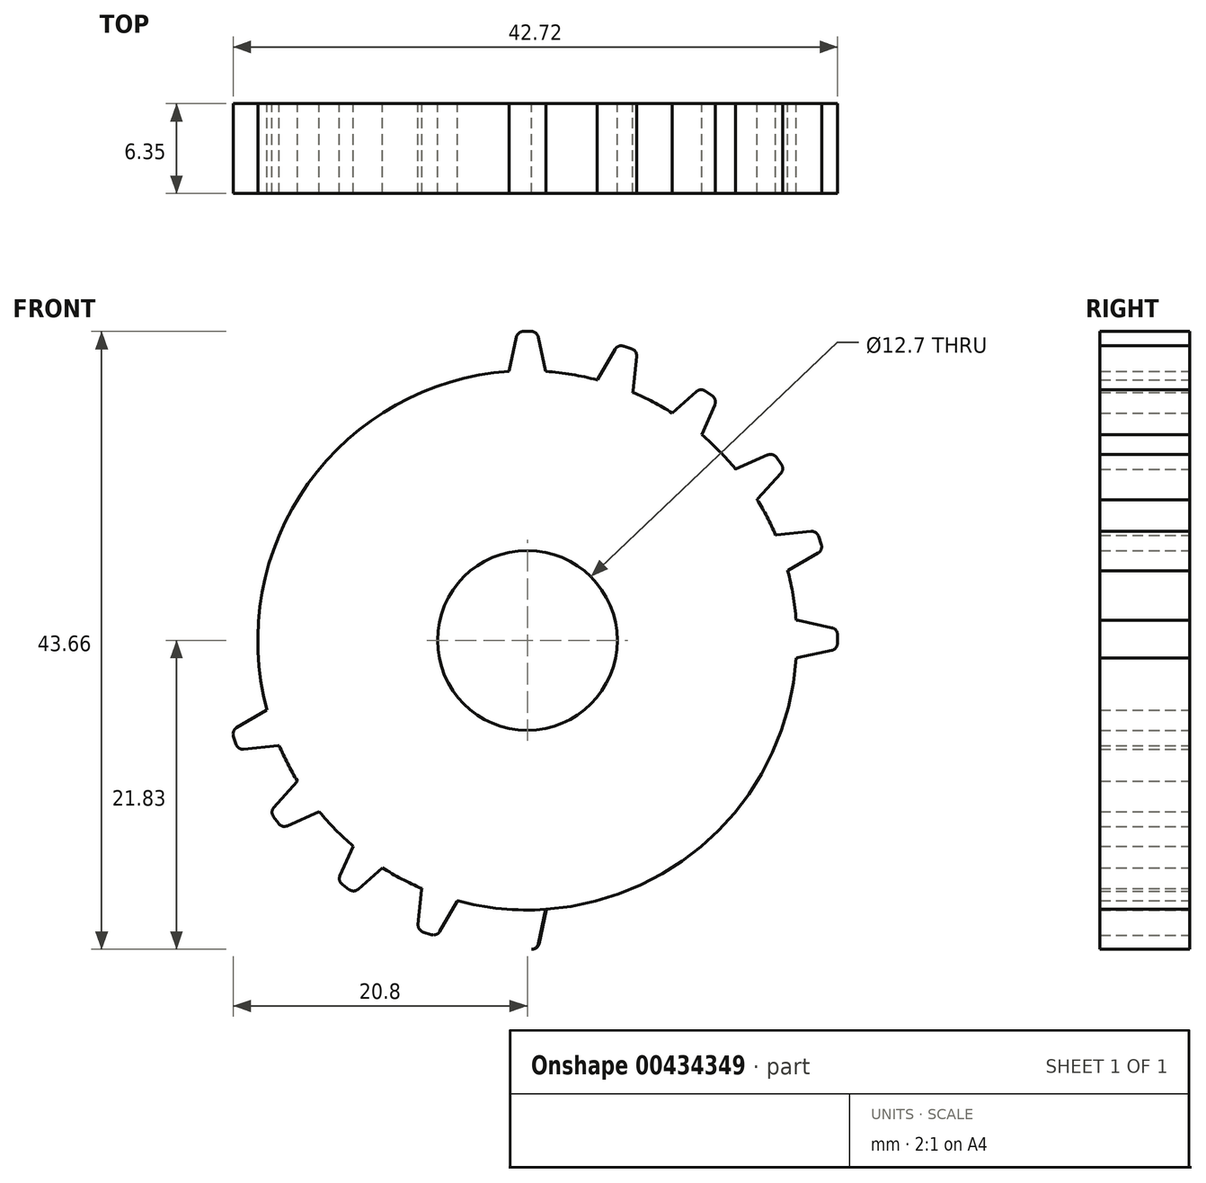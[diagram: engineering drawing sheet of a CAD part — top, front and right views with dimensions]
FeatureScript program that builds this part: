
annotation { "Feature Type Name" : "Feature", "Feature Type Description" : "" }
export const myFeature = defineFeature(function(context is Context, id is Id, definition is map)
    precondition{}
    {
        {
            var Q0;
            Q0=qCreatedBy(makeId("Front.planeOp"),FACE);
            var sketch = newSketch(context, id + "F0", { "sketchPlane" : qUnion([Q0])});
            skCircle(sketch, "E0", {"center": v(0, 0) * mm, "radius": 19.05 * mm});
            skCircle(sketch, "E1", {"center": v(0, 0) * mm, "radius": 6.35 * mm});
            skLineSegment(sketch, "E2", {"start": v(-19.05, 0) * mm, "end": v(19.05, 0) * mm, "construction": true});
            skLineSegment(sketch, "E3", {"start": v(0, 19.05) * mm, "end": v(0, -19.05) * mm, "construction": true});
            skSolve(sketch);
        }
        {
            var Q0;
            Q0 = qSketchRegion(id + "F0", true);
            extrude(context, id + "F1", {"entities" : qUnion([Q0]), "depth" : 6.35 * mm});
        }
        {
            var Q0;
            Q0=qCreatedBy(makeId("Front.planeOp"),FACE);
            var sketch = newSketch(context, id + "F2", { "sketchPlane" : qUnion([Q0])});
            skLineSegment(sketch, "E4", {"start": v(41.5, 29.9) * mm, "end": v(42.1, 29.9) * mm});
            skLineSegment(sketch, "E5", {"start": v(40.48, 27.1) * mm, "end": v(41, 29.5) * mm});
            skLineSegment(sketch, "E6.MirrorCS", {"start": v(43.12, 27.1) * mm, "end": v(42.6, 29.5) * mm});
            skLineSegment(sketch, "E7", {"start": v(40.98, 26.49) * mm, "end": v(42.62, 26.49) * mm});
            skPoint(sketch, "E8.visualSharp", {"position": v(41.08, 29.9) * mm});
            skArc(sketch, "E8.filletArc", {"start": v(41.5, 29.9) * mm, "mid": v(41.18, 29.79) * mm, "end": v(41, 29.5) * mm});
            skPoint(sketch, "E9.visualSharp", {"position": v(42.51, 29.9) * mm});
            skArc(sketch, "E9.filletArc", {"start": v(42.6, 29.5) * mm, "mid": v(42.42, 29.79) * mm, "end": v(42.1, 29.9) * mm});
            skPoint(sketch, "E10.visualSharp", {"position": v(43.25, 26.49) * mm});
            skArc(sketch, "E10.filletArc", {"start": v(42.62, 26.49) * mm, "mid": v(43.02, 26.68) * mm, "end": v(43.12, 27.1) * mm});
            skPoint(sketch, "E11.visualSharp", {"position": v(40.35, 26.49) * mm});
            skArc(sketch, "E11.filletArc", {"start": v(40.48, 27.1) * mm, "mid": v(40.58, 26.68) * mm, "end": v(40.98, 26.49) * mm});
            skLineSegment(sketch, "E12", {"start": v(42.38, 6) * mm, "end": v(42.38, 5.39) * mm});
            skLineSegment(sketch, "E13", {"start": v(39.58, 7.01) * mm, "end": v(41.98, 6.5) * mm});
            skLineSegment(sketch, "E14.MirrorCS", {"start": v(39.58, 4.37) * mm, "end": v(41.98, 4.9) * mm});
            skLineSegment(sketch, "E15", {"start": v(38.97, 6.52) * mm, "end": v(38.97, 4.87) * mm});
            skPoint(sketch, "E16.visualSharp", {"position": v(42.38, 6.4) * mm});
            skArc(sketch, "E16.filletArc", {"start": v(42.38, 6) * mm, "mid": v(42.27, 6.32) * mm, "end": v(41.98, 6.5) * mm});
            skPoint(sketch, "E17.visualSharp", {"position": v(42.38, 4.98) * mm});
            skArc(sketch, "E17.filletArc", {"start": v(41.98, 4.9) * mm, "mid": v(42.27, 5.07) * mm, "end": v(42.38, 5.39) * mm});
            skPoint(sketch, "E18.visualSharp", {"position": v(38.97, 4.24) * mm});
            skArc(sketch, "E18.filletArc", {"start": v(38.97, 4.87) * mm, "mid": v(39.16, 4.48) * mm, "end": v(39.58, 4.37) * mm});
            skPoint(sketch, "E19.visualSharp", {"position": v(38.97, 7.15) * mm});
            skArc(sketch, "E19.filletArc", {"start": v(39.58, 7.01) * mm, "mid": v(39.16, 6.91) * mm, "end": v(38.97, 6.52) * mm});
            skArc(sketch, "E20.MirrorCS", {"start": v(20.55, -6.17) * mm, "mid": v(20.77, -6.43) * mm, "end": v(20.77, -6.77) * mm});
            skArc(sketch, "E21.MirrorCS", {"start": v(6.8, -20.8) * mm, "mid": v(6.45, -20.79) * mm, "end": v(6.2, -20.57) * mm});
            skArc(sketch, "E22.MirrorCS", {"start": v(17.6, -12.94) * mm, "mid": v(17.31, -13.13) * mm, "end": v(16.97, -13.1) * mm});
            skLineSegment(sketch, "E23.MirrorCS", {"start": v(-0.33, -21.83) * mm, "end": v(0.28, -21.83) * mm});
            skLineSegment(sketch, "E24.MirrorCS", {"start": v(17.6, -12.94) * mm, "end": v(17.95, -12.44) * mm});
            skArc(sketch, "E25.MirrorCS", {"start": v(7.72, -20.07) * mm, "mid": v(7.64, -20.4) * mm, "end": v(7.37, -20.6) * mm});
            skArc(sketch, "E26.MirrorCS", {"start": v(17.92, -11.8) * mm, "mid": v(18.04, -12.12) * mm, "end": v(17.95, -12.44) * mm});
            skArc(sketch, "E27.MirrorCS", {"start": v(12.59, -17.61) * mm, "mid": v(12.26, -17.7) * mm, "end": v(11.95, -17.58) * mm});
            skArc(sketch, "E28.MirrorCS", {"start": v(0.78, -21.43) * mm, "mid": v(0.6, -21.72) * mm, "end": v(0.28, -21.83) * mm});
            skArc(sketch, "E29.MirrorCS", {"start": v(-0.33, -21.83) * mm, "mid": v(-0.64, -21.72) * mm, "end": v(-0.82, -21.43) * mm});
            skArc(sketch, "E30.MirrorCS", {"start": v(20.59, -7.35) * mm, "mid": v(20.38, -7.62) * mm, "end": v(20.05, -7.7) * mm});
            skArc(sketch, "E31.MirrorCS", {"start": v(13.25, -16.64) * mm, "mid": v(13.27, -16.98) * mm, "end": v(13.08, -17.25) * mm});
            skLineSegment(sketch, "E32.MirrorCS", {"start": v(20.59, -7.35) * mm, "end": v(20.77, -6.77) * mm});
            skLineSegment(sketch, "E33.MirrorCS", {"start": v(12.59, -17.61) * mm, "end": v(13.08, -17.25) * mm});
            skLineSegment(sketch, "E34.MirrorCS", {"start": v(6.8, -20.8) * mm, "end": v(7.37, -20.6) * mm});
            skArc(sketch, "E35.MirrorCS", {"start": v(17.7, -5.22) * mm, "mid": v(18, -4.9) * mm, "end": v(18.43, -4.94) * mm});
            skLineSegment(sketch, "E36.MirrorCS", {"start": v(14.53, -11.35) * mm, "end": v(15.5, -10.02) * mm});
            skLineSegment(sketch, "E37.MirrorCS", {"start": v(10.16, -15.16) * mm, "end": v(11.5, -14.2) * mm});
            skArc(sketch, "E38.MirrorCS", {"start": v(-1.34, -19.03) * mm, "mid": v(-1.24, -18.6) * mm, "end": v(-0.84, -18.42) * mm});
            skArc(sketch, "E39.MirrorCS", {"start": v(11.5, -14.2) * mm, "mid": v(11.92, -14.11) * mm, "end": v(12.26, -14.4) * mm});
            skArc(sketch, "E40.MirrorCS", {"start": v(0.8, -18.42) * mm, "mid": v(1.2, -18.6) * mm, "end": v(1.3, -19.03) * mm});
            skLineSegment(sketch, "E41.MirrorCS", {"start": v(5.25, -17.71) * mm, "end": v(6.81, -17.2) * mm});
            skLineSegment(sketch, "E42.MirrorCS", {"start": v(17.18, -6.79) * mm, "end": v(17.7, -5.22) * mm});
            skArc(sketch, "E43.MirrorCS", {"start": v(4.96, -18.45) * mm, "mid": v(4.93, -18.01) * mm, "end": v(5.25, -17.71) * mm});
            skArc(sketch, "E44.MirrorCS", {"start": v(15.5, -10.02) * mm, "mid": v(15.88, -9.81) * mm, "end": v(16.28, -9.98) * mm});
            skArc(sketch, "E45.MirrorCS", {"start": v(6.81, -17.2) * mm, "mid": v(7.24, -17.26) * mm, "end": v(7.47, -17.63) * mm});
            skArc(sketch, "E46.MirrorCS", {"start": v(10.12, -15.95) * mm, "mid": v(9.95, -15.54) * mm, "end": v(10.16, -15.16) * mm});
            skArc(sketch, "E47.MirrorCS", {"start": v(17.61, -7.45) * mm, "mid": v(17.24, -7.22) * mm, "end": v(17.18, -6.79) * mm});
            skArc(sketch, "E48.MirrorCS", {"start": v(14.73, -12.11) * mm, "mid": v(14.45, -11.78) * mm, "end": v(14.53, -11.35) * mm});
            skPoint(sketch, "E49.MirrorP", {"position": v(1.43, -18.42) * mm});
            skPoint(sketch, "E50.MirrorP", {"position": v(7.4, -17) * mm});
            skPoint(sketch, "E51.MirrorP", {"position": v(12, -13.82) * mm});
            skPoint(sketch, "E52.MirrorP", {"position": v(17.89, -4.63) * mm});
            skPoint(sketch, "E53.MirrorP", {"position": v(15.86, -9.51) * mm});
            skPoint(sketch, "E54.MirrorP", {"position": v(9.65, -15.53) * mm});
            skPoint(sketch, "E55.MirrorP", {"position": v(20.9, -6.38) * mm});
            skLineSegment(sketch, "E56.MirrorCS", {"start": v(12.26, -14.4) * mm, "end": v(13.25, -16.64) * mm});
            skLineSegment(sketch, "E57.MirrorCS", {"start": v(7.47, -17.63) * mm, "end": v(7.72, -20.07) * mm});
            skLineSegment(sketch, "E58.MirrorCS", {"start": v(16.28, -9.98) * mm, "end": v(17.92, -11.8) * mm});
            skLineSegment(sketch, "E59.MirrorCS", {"start": v(10.12, -15.95) * mm, "end": v(11.95, -17.58) * mm});
            skLineSegment(sketch, "E60.MirrorCS", {"start": v(-1.34, -19.03) * mm, "end": v(-0.82, -21.43) * mm});
            skPoint(sketch, "E61.MirrorP", {"position": v(0.7, -21.83) * mm});
            skPoint(sketch, "E62.MirrorP", {"position": v(7.76, -20.48) * mm});
            skPoint(sketch, "E63.MirrorP", {"position": v(18.19, -12.11) * mm});
            skLineSegment(sketch, "E64.MirrorCS", {"start": v(4.96, -18.45) * mm, "end": v(6.2, -20.57) * mm});
            skLineSegment(sketch, "E65.MirrorCS", {"start": v(14.73, -12.11) * mm, "end": v(16.97, -13.1) * mm});
            skPoint(sketch, "E66.MirrorP", {"position": v(-0.74, -21.83) * mm});
            skPoint(sketch, "E67.MirrorP", {"position": v(6.4, -20.92) * mm});
            skPoint(sketch, "E68.MirrorP", {"position": v(17.35, -13.27) * mm});
            skPoint(sketch, "E69.MirrorP", {"position": v(14.16, -11.86) * mm});
            skPoint(sketch, "E70.MirrorP", {"position": v(16.99, -7.39) * mm});
            skLineSegment(sketch, "E71.MirrorCS", {"start": v(-0.84, -18.42) * mm, "end": v(0.8, -18.42) * mm});
            skLineSegment(sketch, "E72.MirrorCS", {"start": v(1.3, -19.03) * mm, "end": v(0.78, -21.43) * mm});
            skLineSegment(sketch, "E73.MirrorCS", {"start": v(17.61, -7.45) * mm, "end": v(20.05, -7.7) * mm});
            skLineSegment(sketch, "E74.MirrorCS", {"start": v(18.43, -4.94) * mm, "end": v(20.55, -6.17) * mm});
            skPoint(sketch, "E75.MirrorP", {"position": v(12.26, -17.85) * mm});
            skPoint(sketch, "E76.MirrorP", {"position": v(20.46, -7.74) * mm});
            skPoint(sketch, "E77.MirrorP", {"position": v(13.41, -17.01) * mm});
            skPoint(sketch, "E78.MirrorP", {"position": v(-1.47, -18.42) * mm});
            skPoint(sketch, "E79.MirrorP", {"position": v(4.65, -17.9) * mm});
            skArc(sketch, "E80.MirrorCS", {"start": v(0.33, -21.83) * mm, "mid": v(0.64, -21.72) * mm, "end": v(0.82, -21.43) * mm});
            skLineSegment(sketch, "E81.MirrorCS", {"start": v(-12.59, -17.61) * mm, "end": v(-13.08, -17.25) * mm});
            skLineSegment(sketch, "E82.MirrorCS", {"start": v(-6.8, -20.8) * mm, "end": v(-7.37, -20.6) * mm});
            skArc(sketch, "E83.MirrorCS", {"start": v(-20.55, -6.17) * mm, "mid": v(-20.77, -6.43) * mm, "end": v(-20.77, -6.77) * mm});
            skArc(sketch, "E84.MirrorCS", {"start": v(-20.59, -7.35) * mm, "mid": v(-20.38, -7.62) * mm, "end": v(-20.05, -7.7) * mm});
            skLineSegment(sketch, "E85.MirrorCS", {"start": v(-17.6, -12.94) * mm, "end": v(-17.95, -12.44) * mm});
            skLineSegment(sketch, "E86.MirrorCS", {"start": v(-20.59, -7.35) * mm, "end": v(-20.77, -6.77) * mm});
            skArc(sketch, "E87.MirrorCS", {"start": v(-17.92, -11.8) * mm, "mid": v(-18.04, -12.12) * mm, "end": v(-17.95, -12.44) * mm});
            skArc(sketch, "E88.MirrorCS", {"start": v(-7.72, -20.07) * mm, "mid": v(-7.64, -20.4) * mm, "end": v(-7.37, -20.6) * mm});
            skArc(sketch, "E89.MirrorCS", {"start": v(-6.8, -20.8) * mm, "mid": v(-6.45, -20.79) * mm, "end": v(-6.2, -20.57) * mm});
            skLineSegment(sketch, "E90.MirrorCS", {"start": v(0.33, -21.83) * mm, "end": v(-0.28, -21.83) * mm});
            skArc(sketch, "E91.MirrorCS", {"start": v(-13.25, -16.64) * mm, "mid": v(-13.27, -16.98) * mm, "end": v(-13.08, -17.25) * mm});
            skArc(sketch, "E92.MirrorCS", {"start": v(-12.59, -17.61) * mm, "mid": v(-12.26, -17.7) * mm, "end": v(-11.95, -17.58) * mm});
            skArc(sketch, "E93.MirrorCS", {"start": v(-0.78, -21.43) * mm, "mid": v(-0.6, -21.72) * mm, "end": v(-0.28, -21.83) * mm});
            skArc(sketch, "E94.MirrorCS", {"start": v(-17.6, -12.94) * mm, "mid": v(-17.31, -13.13) * mm, "end": v(-16.97, -13.1) * mm});
            skArc(sketch, "E95.MirrorCS", {"start": v(-11.5, -14.2) * mm, "mid": v(-11.92, -14.11) * mm, "end": v(-12.26, -14.4) * mm});
            skArc(sketch, "E96.MirrorCS", {"start": v(-14.73, -12.11) * mm, "mid": v(-14.45, -11.78) * mm, "end": v(-14.53, -11.35) * mm});
            skArc(sketch, "E97.MirrorCS", {"start": v(-17.7, -5.22) * mm, "mid": v(-18, -4.9) * mm, "end": v(-18.43, -4.94) * mm});
            skArc(sketch, "E98.MirrorCS", {"start": v(-0.8, -18.42) * mm, "mid": v(-1.2, -18.6) * mm, "end": v(-1.3, -19.03) * mm});
            skLineSegment(sketch, "E99.MirrorCS", {"start": v(-14.53, -11.35) * mm, "end": v(-15.5, -10.02) * mm});
            skArc(sketch, "E100.MirrorCS", {"start": v(-10.12, -15.95) * mm, "mid": v(-9.95, -15.54) * mm, "end": v(-10.16, -15.16) * mm});
            skLineSegment(sketch, "E101.MirrorCS", {"start": v(-10.16, -15.16) * mm, "end": v(-11.5, -14.2) * mm});
            skLineSegment(sketch, "E102.MirrorCS", {"start": v(-17.18, -6.79) * mm, "end": v(-17.7, -5.22) * mm});
            skLineSegment(sketch, "E103.MirrorCS", {"start": v(-5.25, -17.71) * mm, "end": v(-6.81, -17.2) * mm});
            skArc(sketch, "E104.MirrorCS", {"start": v(-6.81, -17.2) * mm, "mid": v(-7.24, -17.26) * mm, "end": v(-7.47, -17.63) * mm});
            skArc(sketch, "E105.MirrorCS", {"start": v(-17.61, -7.45) * mm, "mid": v(-17.24, -7.22) * mm, "end": v(-17.18, -6.79) * mm});
            skArc(sketch, "E106.MirrorCS", {"start": v(-15.5, -10.02) * mm, "mid": v(-15.88, -9.81) * mm, "end": v(-16.28, -9.98) * mm});
            skArc(sketch, "E107.MirrorCS", {"start": v(1.34, -19.03) * mm, "mid": v(1.24, -18.6) * mm, "end": v(0.84, -18.42) * mm});
            skArc(sketch, "E108.MirrorCS", {"start": v(-4.96, -18.45) * mm, "mid": v(-4.93, -18.01) * mm, "end": v(-5.25, -17.71) * mm});
            skLineSegment(sketch, "E109.MirrorCS", {"start": v(-14.73, -12.11) * mm, "end": v(-16.97, -13.1) * mm});
            skPoint(sketch, "E110.MirrorP", {"position": v(-7.76, -20.48) * mm});
            skPoint(sketch, "E111.MirrorP", {"position": v(-13.41, -17.01) * mm});
            skPoint(sketch, "E112.MirrorP", {"position": v(-15.86, -9.51) * mm});
            skPoint(sketch, "E113.MirrorP", {"position": v(-9.65, -15.53) * mm});
            skLineSegment(sketch, "E114.MirrorCS", {"start": v(-12.26, -14.4) * mm, "end": v(-13.25, -16.64) * mm});
            skPoint(sketch, "E115.MirrorP", {"position": v(0.74, -21.83) * mm});
            skLineSegment(sketch, "E116.MirrorCS", {"start": v(-7.47, -17.63) * mm, "end": v(-7.72, -20.07) * mm});
            skPoint(sketch, "E117.MirrorP", {"position": v(-12.26, -17.85) * mm});
            skPoint(sketch, "E118.MirrorP", {"position": v(-6.4, -20.92) * mm});
            skLineSegment(sketch, "E119.MirrorCS", {"start": v(-16.28, -9.98) * mm, "end": v(-17.92, -11.8) * mm});
            skPoint(sketch, "E120.MirrorP", {"position": v(-12, -13.82) * mm});
            skLineSegment(sketch, "E121.MirrorCS", {"start": v(0.84, -18.42) * mm, "end": v(-0.8, -18.42) * mm});
            skPoint(sketch, "E122.MirrorP", {"position": v(-17.35, -13.27) * mm});
            skPoint(sketch, "E123.MirrorP", {"position": v(-20.9, -6.38) * mm});
            skLineSegment(sketch, "E124.MirrorCS", {"start": v(-10.12, -15.95) * mm, "end": v(-11.95, -17.58) * mm});
            skPoint(sketch, "E125.MirrorP", {"position": v(1.47, -18.42) * mm});
            skPoint(sketch, "E126.MirrorP", {"position": v(-14.16, -11.86) * mm});
            skLineSegment(sketch, "E127.MirrorCS", {"start": v(-17.61, -7.45) * mm, "end": v(-20.05, -7.7) * mm});
            skPoint(sketch, "E128.MirrorP", {"position": v(-18.19, -12.11) * mm});
            skPoint(sketch, "E129.MirrorP", {"position": v(-1.43, -18.42) * mm});
            skPoint(sketch, "E130.MirrorP", {"position": v(-20.46, -7.74) * mm});
            skLineSegment(sketch, "E131.MirrorCS", {"start": v(1.34, -19.03) * mm, "end": v(0.82, -21.43) * mm});
            skLineSegment(sketch, "E132.MirrorCS", {"start": v(-1.3, -19.03) * mm, "end": v(-0.78, -21.43) * mm});
            skPoint(sketch, "E133.MirrorP", {"position": v(-7.4, -17) * mm});
            skPoint(sketch, "E134.MirrorP", {"position": v(-0.7, -21.83) * mm});
            skPoint(sketch, "E135.MirrorP", {"position": v(-16.99, -7.39) * mm});
            skLineSegment(sketch, "E136.MirrorCS", {"start": v(-18.43, -4.94) * mm, "end": v(-20.55, -6.17) * mm});
            skLineSegment(sketch, "E137.MirrorCS", {"start": v(-4.96, -18.45) * mm, "end": v(-6.2, -20.57) * mm});
            skPoint(sketch, "E138.MirrorP", {"position": v(-17.89, -4.63) * mm});
            skPoint(sketch, "E139.MirrorP", {"position": v(-4.65, -17.9) * mm});
            skLineSegment(sketch, "E140.MirrorCS", {"start": v(0.33, 21.83) * mm, "end": v(-0.28, 21.83) * mm});
            skArc(sketch, "E141.MirrorCS", {"start": v(0.33, 21.83) * mm, "mid": v(0.64, 21.72) * mm, "end": v(0.82, 21.43) * mm});
            skArc(sketch, "E142.MirrorCS", {"start": v(0.78, 21.43) * mm, "mid": v(0.6, 21.72) * mm, "end": v(0.28, 21.83) * mm});
            skArc(sketch, "E143.MirrorCS", {"start": v(-0.78, 21.43) * mm, "mid": v(-0.6, 21.72) * mm, "end": v(-0.28, 21.83) * mm});
            skArc(sketch, "E144.MirrorCS", {"start": v(-0.33, 21.83) * mm, "mid": v(-0.64, 21.72) * mm, "end": v(-0.82, 21.43) * mm});
            skLineSegment(sketch, "E145.MirrorCS", {"start": v(-0.33, 21.83) * mm, "end": v(0.28, 21.83) * mm});
            skArc(sketch, "E146.MirrorCS", {"start": v(-1.34, 19.03) * mm, "mid": v(-1.24, 18.6) * mm, "end": v(-0.84, 18.42) * mm});
            skArc(sketch, "E147.MirrorCS", {"start": v(-0.8, 18.42) * mm, "mid": v(-1.2, 18.6) * mm, "end": v(-1.3, 19.03) * mm});
            skLineSegment(sketch, "E148.MirrorCS", {"start": v(-0.84, 18.42) * mm, "end": v(0.8, 18.42) * mm});
            skArc(sketch, "E149.MirrorCS", {"start": v(0.8, 18.42) * mm, "mid": v(1.2, 18.6) * mm, "end": v(1.3, 19.03) * mm});
            skLineSegment(sketch, "E150.MirrorCS", {"start": v(0.84, 18.42) * mm, "end": v(-0.8, 18.42) * mm});
            skArc(sketch, "E151.MirrorCS", {"start": v(1.34, 19.03) * mm, "mid": v(1.24, 18.6) * mm, "end": v(0.84, 18.42) * mm});
            skArc(sketch, "E152.MirrorCS", {"start": v(-15.5, 10.02) * mm, "mid": v(-15.88, 9.81) * mm, "end": v(-16.28, 9.98) * mm});
            skArc(sketch, "E153.MirrorCS", {"start": v(17.6, 12.94) * mm, "mid": v(17.31, 13.13) * mm, "end": v(16.97, 13.1) * mm});
            skArc(sketch, "E154.MirrorCS", {"start": v(-7.72, 20.07) * mm, "mid": v(-7.64, 20.4) * mm, "end": v(-7.37, 20.6) * mm});
            skArc(sketch, "E155.MirrorCS", {"start": v(-17.92, 11.8) * mm, "mid": v(-18.04, 12.12) * mm, "end": v(-17.95, 12.44) * mm});
            skArc(sketch, "E156.MirrorCS", {"start": v(20.59, 7.35) * mm, "mid": v(20.38, 7.62) * mm, "end": v(20.05, 7.7) * mm});
            skLineSegment(sketch, "E157.MirrorCS", {"start": v(-6.8, 20.8) * mm, "end": v(-7.37, 20.6) * mm});
            skArc(sketch, "E158.MirrorCS", {"start": v(20.55, 6.17) * mm, "mid": v(20.77, 6.43) * mm, "end": v(20.77, 6.77) * mm});
            skArc(sketch, "E159.MirrorCS", {"start": v(-12.59, 17.61) * mm, "mid": v(-12.26, 17.7) * mm, "end": v(-11.95, 17.58) * mm});
            skArc(sketch, "E160.MirrorCS", {"start": v(6.8, 20.8) * mm, "mid": v(6.45, 20.79) * mm, "end": v(6.2, 20.57) * mm});
            skArc(sketch, "E161.MirrorCS", {"start": v(13.25, 16.64) * mm, "mid": v(13.27, 16.98) * mm, "end": v(13.08, 17.25) * mm});
            skArc(sketch, "E162.MirrorCS", {"start": v(12.59, 17.61) * mm, "mid": v(12.26, 17.7) * mm, "end": v(11.95, 17.58) * mm});
            skLineSegment(sketch, "E163.MirrorCS", {"start": v(12.59, 17.61) * mm, "end": v(13.08, 17.25) * mm});
            skArc(sketch, "E164.MirrorCS", {"start": v(15.5, 10.02) * mm, "mid": v(15.88, 9.81) * mm, "end": v(16.28, 9.98) * mm});
            skArc(sketch, "E165.MirrorCS", {"start": v(-20.55, 6.17) * mm, "mid": v(-20.77, 6.43) * mm, "end": v(-20.77, 6.77) * mm});
            skLineSegment(sketch, "E166.MirrorCS", {"start": v(20.59, 7.35) * mm, "end": v(20.77, 6.77) * mm});
            skArc(sketch, "E167.MirrorCS", {"start": v(-20.59, 7.35) * mm, "mid": v(-20.38, 7.62) * mm, "end": v(-20.05, 7.7) * mm});
            skLineSegment(sketch, "E168.MirrorCS", {"start": v(6.8, 20.8) * mm, "end": v(7.37, 20.6) * mm});
            skLineSegment(sketch, "E169.MirrorCS", {"start": v(17.6, 12.94) * mm, "end": v(17.95, 12.44) * mm});
            skLineSegment(sketch, "E170.MirrorCS", {"start": v(-17.6, 12.94) * mm, "end": v(-17.95, 12.44) * mm});
            skArc(sketch, "E171.MirrorCS", {"start": v(-17.6, 12.94) * mm, "mid": v(-17.31, 13.13) * mm, "end": v(-16.97, 13.1) * mm});
            skLineSegment(sketch, "E172.MirrorCS", {"start": v(-20.59, 7.35) * mm, "end": v(-20.77, 6.77) * mm});
            skArc(sketch, "E173.MirrorCS", {"start": v(17.92, 11.8) * mm, "mid": v(18.04, 12.12) * mm, "end": v(17.95, 12.44) * mm});
            skArc(sketch, "E174.MirrorCS", {"start": v(-13.25, 16.64) * mm, "mid": v(-13.27, 16.98) * mm, "end": v(-13.08, 17.25) * mm});
            skArc(sketch, "E175.MirrorCS", {"start": v(-6.8, 20.8) * mm, "mid": v(-6.45, 20.79) * mm, "end": v(-6.2, 20.57) * mm});
            skArc(sketch, "E176.MirrorCS", {"start": v(-6.81, 17.2) * mm, "mid": v(-7.24, 17.26) * mm, "end": v(-7.47, 17.63) * mm});
            skLineSegment(sketch, "E177.MirrorCS", {"start": v(-5.25, 17.71) * mm, "end": v(-6.81, 17.2) * mm});
            skArc(sketch, "E178.MirrorCS", {"start": v(17.7, 5.22) * mm, "mid": v(18, 4.9) * mm, "end": v(18.43, 4.94) * mm});
            skArc(sketch, "E179.MirrorCS", {"start": v(10.12, 15.95) * mm, "mid": v(9.95, 15.54) * mm, "end": v(10.16, 15.16) * mm});
            skLineSegment(sketch, "E180.MirrorCS", {"start": v(14.53, 11.35) * mm, "end": v(15.5, 10.02) * mm});
            skLineSegment(sketch, "E181.MirrorCS", {"start": v(-14.53, 11.35) * mm, "end": v(-15.5, 10.02) * mm});
            skArc(sketch, "E182.MirrorCS", {"start": v(-11.5, 14.2) * mm, "mid": v(-11.92, 14.11) * mm, "end": v(-12.26, 14.4) * mm});
            skArc(sketch, "E183.MirrorCS", {"start": v(-4.96, 18.45) * mm, "mid": v(-4.93, 18.01) * mm, "end": v(-5.25, 17.71) * mm});
            skArc(sketch, "E184.MirrorCS", {"start": v(-14.73, 12.11) * mm, "mid": v(-14.45, 11.78) * mm, "end": v(-14.53, 11.35) * mm});
            skLineSegment(sketch, "E185.MirrorCS", {"start": v(5.25, 17.71) * mm, "end": v(6.81, 17.2) * mm});
            skArc(sketch, "E186.MirrorCS", {"start": v(7.72, 20.07) * mm, "mid": v(7.64, 20.4) * mm, "end": v(7.37, 20.6) * mm});
            skArc(sketch, "E187.MirrorCS", {"start": v(-10.12, 15.95) * mm, "mid": v(-9.95, 15.54) * mm, "end": v(-10.16, 15.16) * mm});
            skArc(sketch, "E188.MirrorCS", {"start": v(14.73, 12.11) * mm, "mid": v(14.45, 11.78) * mm, "end": v(14.53, 11.35) * mm});
            skArc(sketch, "E189.MirrorCS", {"start": v(-17.61, 7.45) * mm, "mid": v(-17.24, 7.22) * mm, "end": v(-17.18, 6.79) * mm});
            skArc(sketch, "E190.MirrorCS", {"start": v(17.61, 7.45) * mm, "mid": v(17.24, 7.22) * mm, "end": v(17.18, 6.79) * mm});
            skArc(sketch, "E191.MirrorCS", {"start": v(4.96, 18.45) * mm, "mid": v(4.93, 18.01) * mm, "end": v(5.25, 17.71) * mm});
            skLineSegment(sketch, "E192.MirrorCS", {"start": v(10.16, 15.16) * mm, "end": v(11.5, 14.2) * mm});
            skArc(sketch, "E193.MirrorCS", {"start": v(-17.7, 5.22) * mm, "mid": v(-18, 4.9) * mm, "end": v(-18.43, 4.94) * mm});
            skLineSegment(sketch, "E194.MirrorCS", {"start": v(-10.16, 15.16) * mm, "end": v(-11.5, 14.2) * mm});
            skLineSegment(sketch, "E195.MirrorCS", {"start": v(-12.59, 17.61) * mm, "end": v(-13.08, 17.25) * mm});
            skArc(sketch, "E196.MirrorCS", {"start": v(6.81, 17.2) * mm, "mid": v(7.24, 17.26) * mm, "end": v(7.47, 17.63) * mm});
            skLineSegment(sketch, "E197.MirrorCS", {"start": v(-17.18, 6.79) * mm, "end": v(-17.7, 5.22) * mm});
            skLineSegment(sketch, "E198.MirrorCS", {"start": v(17.18, 6.79) * mm, "end": v(17.7, 5.22) * mm});
            skArc(sketch, "E199.MirrorCS", {"start": v(11.5, 14.2) * mm, "mid": v(11.92, 14.11) * mm, "end": v(12.26, 14.4) * mm});
            skPoint(sketch, "E200.MirrorP", {"position": v(0.7, 21.83) * mm});
            skPoint(sketch, "E201.MirrorP", {"position": v(-0.74, 21.83) * mm});
            skPoint(sketch, "E202.MirrorP", {"position": v(-1.47, 18.42) * mm});
            skPoint(sketch, "E203.MirrorP", {"position": v(1.43, 18.42) * mm});
            skLineSegment(sketch, "E204.MirrorCS", {"start": v(-1.3, 19.03) * mm, "end": v(-0.78, 21.43) * mm});
            skPoint(sketch, "E205.MirrorP", {"position": v(17.35, 13.27) * mm});
            skPoint(sketch, "E206.MirrorP", {"position": v(0.74, 21.83) * mm});
            skLineSegment(sketch, "E207.MirrorCS", {"start": v(4.96, 18.45) * mm, "end": v(6.2, 20.57) * mm});
            skLineSegment(sketch, "E208.MirrorCS", {"start": v(10.12, 15.95) * mm, "end": v(11.95, 17.58) * mm});
            skLineSegment(sketch, "E209.MirrorCS", {"start": v(16.28, 9.98) * mm, "end": v(17.92, 11.8) * mm});
            skLineSegment(sketch, "E210.MirrorCS", {"start": v(-4.96, 18.45) * mm, "end": v(-6.2, 20.57) * mm});
            skPoint(sketch, "E211.MirrorP", {"position": v(16.99, 7.39) * mm});
            skPoint(sketch, "E212.MirrorP", {"position": v(-6.4, 20.92) * mm});
            skPoint(sketch, "E213.MirrorP", {"position": v(-4.65, 17.9) * mm});
            skPoint(sketch, "E214.MirrorP", {"position": v(18.19, 12.11) * mm});
            skPoint(sketch, "E215.MirrorP", {"position": v(-13.41, 17.01) * mm});
            skPoint(sketch, "E216.MirrorP", {"position": v(6.4, 20.92) * mm});
            skPoint(sketch, "E217.MirrorP", {"position": v(-9.65, 15.53) * mm});
            skPoint(sketch, "E218.MirrorP", {"position": v(20.9, 6.38) * mm});
            skLineSegment(sketch, "E219.MirrorCS", {"start": v(-10.12, 15.95) * mm, "end": v(-11.95, 17.58) * mm});
            skPoint(sketch, "E220.MirrorP", {"position": v(-7.76, 20.48) * mm});
            skPoint(sketch, "E221.MirrorP", {"position": v(-0.7, 21.83) * mm});
            skPoint(sketch, "E222.MirrorP", {"position": v(7.76, 20.48) * mm});
            skPoint(sketch, "E223.MirrorP", {"position": v(-20.46, 7.74) * mm});
            skPoint(sketch, "E224.MirrorP", {"position": v(-17.35, 13.27) * mm});
            skLineSegment(sketch, "E225.MirrorCS", {"start": v(18.43, 4.94) * mm, "end": v(20.55, 6.17) * mm});
            skLineSegment(sketch, "E226.MirrorCS", {"start": v(-17.61, 7.45) * mm, "end": v(-20.05, 7.7) * mm});
            skLineSegment(sketch, "E227.MirrorCS", {"start": v(-7.47, 17.63) * mm, "end": v(-7.72, 20.07) * mm});
            skPoint(sketch, "E228.MirrorP", {"position": v(-20.9, 6.38) * mm});
            skPoint(sketch, "E229.MirrorP", {"position": v(-18.19, 12.11) * mm});
            skPoint(sketch, "E230.MirrorP", {"position": v(-7.4, 17) * mm});
            skLineSegment(sketch, "E231.MirrorCS", {"start": v(-16.28, 9.98) * mm, "end": v(-17.92, 11.8) * mm});
            skPoint(sketch, "E232.MirrorP", {"position": v(-12.26, 17.85) * mm});
            skPoint(sketch, "E233.MirrorP", {"position": v(14.16, 11.86) * mm});
            skLineSegment(sketch, "E234.MirrorCS", {"start": v(-14.73, 12.11) * mm, "end": v(-16.97, 13.1) * mm});
            skPoint(sketch, "E235.MirrorP", {"position": v(-15.86, 9.51) * mm});
            skPoint(sketch, "E236.MirrorP", {"position": v(-17.89, 4.63) * mm});
            skPoint(sketch, "E237.MirrorP", {"position": v(9.65, 15.53) * mm});
            skPoint(sketch, "E238.MirrorP", {"position": v(1.47, 18.42) * mm});
            skPoint(sketch, "E239.MirrorP", {"position": v(20.46, 7.74) * mm});
            skLineSegment(sketch, "E240.MirrorCS", {"start": v(1.34, 19.03) * mm, "end": v(0.82, 21.43) * mm});
            skPoint(sketch, "E241.MirrorP", {"position": v(4.65, 17.9) * mm});
            skPoint(sketch, "E242.MirrorP", {"position": v(17.89, 4.63) * mm});
            skPoint(sketch, "E243.MirrorP", {"position": v(-14.16, 11.86) * mm});
            skPoint(sketch, "E244.MirrorP", {"position": v(-1.43, 18.42) * mm});
            skPoint(sketch, "E245.MirrorP", {"position": v(-16.99, 7.39) * mm});
            skLineSegment(sketch, "E246.MirrorCS", {"start": v(-18.43, 4.94) * mm, "end": v(-20.55, 6.17) * mm});
            skPoint(sketch, "E247.MirrorP", {"position": v(15.86, 9.51) * mm});
            skLineSegment(sketch, "E248.MirrorCS", {"start": v(1.3, 19.03) * mm, "end": v(0.78, 21.43) * mm});
            skPoint(sketch, "E249.MirrorP", {"position": v(12.26, 17.85) * mm});
            skPoint(sketch, "E250.MirrorP", {"position": v(-12, 13.82) * mm});
            skPoint(sketch, "E251.MirrorP", {"position": v(12, 13.82) * mm});
            skLineSegment(sketch, "E252.MirrorCS", {"start": v(-12.26, 14.4) * mm, "end": v(-13.25, 16.64) * mm});
            skPoint(sketch, "E253.MirrorP", {"position": v(7.4, 17) * mm});
            skPoint(sketch, "E254.MirrorP", {"position": v(13.41, 17.01) * mm});
            skLineSegment(sketch, "E255.MirrorCS", {"start": v(7.47, 17.63) * mm, "end": v(7.72, 20.07) * mm});
            skLineSegment(sketch, "E256.MirrorCS", {"start": v(14.73, 12.11) * mm, "end": v(16.97, 13.1) * mm});
            skLineSegment(sketch, "E257.MirrorCS", {"start": v(12.26, 14.4) * mm, "end": v(13.25, 16.64) * mm});
            skLineSegment(sketch, "E258.MirrorCS", {"start": v(17.61, 7.45) * mm, "end": v(20.05, 7.7) * mm});
            skLineSegment(sketch, "E259.MirrorCS", {"start": v(-1.34, 19.03) * mm, "end": v(-0.82, 21.43) * mm});
            skArc(sketch, "E260.MirrorCS", {"start": v(42.38, -6) * mm, "mid": v(42.27, -6.32) * mm, "end": v(41.98, -6.5) * mm});
            skArc(sketch, "E261.MirrorCS", {"start": v(41.98, -4.9) * mm, "mid": v(42.27, -5.07) * mm, "end": v(42.38, -5.39) * mm});
            skLineSegment(sketch, "E262.MirrorCS", {"start": v(42.38, -6) * mm, "end": v(42.38, -5.39) * mm});
            skArc(sketch, "E263.MirrorCS", {"start": v(38.97, -4.87) * mm, "mid": v(39.16, -4.48) * mm, "end": v(39.58, -4.37) * mm});
            skArc(sketch, "E264.MirrorCS", {"start": v(39.58, -7.01) * mm, "mid": v(39.16, -6.91) * mm, "end": v(38.97, -6.52) * mm});
            skLineSegment(sketch, "E265.MirrorCS", {"start": v(38.97, -6.52) * mm, "end": v(38.97, -4.87) * mm});
            skPoint(sketch, "E266.MirrorP", {"position": v(42.38, -6.4) * mm});
            skPoint(sketch, "E267.MirrorP", {"position": v(42.38, -4.98) * mm});
            skPoint(sketch, "E268.MirrorP", {"position": v(38.97, -7.15) * mm});
            skPoint(sketch, "E269.MirrorP", {"position": v(38.97, -4.24) * mm});
            skLineSegment(sketch, "E270.MirrorCS", {"start": v(39.58, -4.37) * mm, "end": v(41.98, -4.9) * mm});
            skLineSegment(sketch, "E271.MirrorCS", {"start": v(39.58, -7.01) * mm, "end": v(41.98, -6.5) * mm});
            skLineSegment(sketch, "E272", {"start": v(21.92, 0.4) * mm, "end": v(21.92, -0.2) * mm});
            skLineSegment(sketch, "E273", {"start": v(19.12, 1.41) * mm, "end": v(21.52, 0.9) * mm});
            skLineSegment(sketch, "E274.MirrorCS", {"start": v(19.12, -1.22) * mm, "end": v(21.52, -0.7) * mm});
            skLineSegment(sketch, "E275", {"start": v(18.5, 0.92) * mm, "end": v(18.5, -0.73) * mm});
            skPoint(sketch, "E276.visualSharp", {"position": v(21.92, 0.81) * mm});
            skArc(sketch, "E276.filletArc", {"start": v(21.92, 0.4) * mm, "mid": v(21.8, 0.72) * mm, "end": v(21.52, 0.9) * mm});
            skPoint(sketch, "E277.visualSharp", {"position": v(21.92, -0.62) * mm});
            skArc(sketch, "E277.filletArc", {"start": v(21.52, -0.7) * mm, "mid": v(21.8, -0.53) * mm, "end": v(21.92, -0.2) * mm});
            skPoint(sketch, "E278.visualSharp", {"position": v(18.5, -1.36) * mm});
            skArc(sketch, "E278.filletArc", {"start": v(18.5, -0.73) * mm, "mid": v(18.7, -1.12) * mm, "end": v(19.12, -1.22) * mm});
            skPoint(sketch, "E279.visualSharp", {"position": v(18.5, 1.55) * mm});
            skArc(sketch, "E279.filletArc", {"start": v(19.12, 1.41) * mm, "mid": v(18.7, 1.31) * mm, "end": v(18.5, 0.92) * mm});
            skArc(sketch, "E280.MirrorCS", {"start": v(-21.52, -0.7) * mm, "mid": v(-21.8, -0.53) * mm, "end": v(-21.92, -0.2) * mm});
            skArc(sketch, "E281.MirrorCS", {"start": v(-21.92, 0.4) * mm, "mid": v(-21.8, 0.72) * mm, "end": v(-21.52, 0.9) * mm});
            skLineSegment(sketch, "E282.MirrorCS", {"start": v(-18.5, 0.92) * mm, "end": v(-18.5, -0.73) * mm});
            skLineSegment(sketch, "E283.MirrorCS", {"start": v(-21.92, 0.4) * mm, "end": v(-21.92, -0.2) * mm});
            skArc(sketch, "E284.MirrorCS", {"start": v(-18.5, -0.73) * mm, "mid": v(-18.7, -1.12) * mm, "end": v(-19.12, -1.22) * mm});
            skArc(sketch, "E285.MirrorCS", {"start": v(-19.12, 1.41) * mm, "mid": v(-18.7, 1.31) * mm, "end": v(-18.5, 0.92) * mm});
            skLineSegment(sketch, "E286.MirrorCS", {"start": v(-19.12, -1.22) * mm, "end": v(-21.52, -0.7) * mm});
            skPoint(sketch, "E287.MirrorP", {"position": v(-18.5, 1.55) * mm});
            skLineSegment(sketch, "E288.MirrorCS", {"start": v(-19.12, 1.41) * mm, "end": v(-21.52, 0.9) * mm});
            skPoint(sketch, "E289.MirrorP", {"position": v(-18.5, -1.36) * mm});
            skPoint(sketch, "E290.MirrorP", {"position": v(-21.92, -0.62) * mm});
            skPoint(sketch, "E291.MirrorP", {"position": v(-21.92, 0.81) * mm});
            skSolve(sketch);
        }
        {
            var Q0;
            Q0=makeQuery(id+"F2.imprint","IMPRINT",FACE,{"disambiguationData":[TD([[makeQuery(id+"F2.imprint","IMPRINT",EDGE,{"derivedFrom":sQuery(id+"F2.wireOp",EDGE,"E159.MirrorCS")}),-1.0]])]});
            var Q1;
            Q1=makeQuery(id+"F2.imprint","IMPRINT",FACE,{"disambiguationData":[TD([[makeQuery(id+"F2.imprint","IMPRINT",EDGE,{"derivedFrom":sQuery(id+"F2.wireOp",EDGE,"E154.MirrorCS")}),-1.0]])]});
            var Q2;
            {var subQ1=sQuery(id+"F2.wireOp",EDGE,"E142.MirrorCS");Q2=makeQuery(id+"F2.imprint","IMPRINT",FACE,{"disambiguationData":[TD([[makeQuery(id+"F2.imprint","IMPRINT",EDGE,{"derivedFrom":subQ1}),1.0]])]});}
            var Q3;
            Q3=makeQuery(id+"F2.imprint","IMPRINT",FACE,{"disambiguationData":[TD([[makeQuery(id+"F2.imprint","IMPRINT",EDGE,{"derivedFrom":sQuery(id+"F2.wireOp",EDGE,"E160.MirrorCS")}),1.0]])]});
            var Q4;
            Q4=makeQuery(id+"F2.imprint","IMPRINT",FACE,{"disambiguationData":[TD([[makeQuery(id+"F2.imprint","IMPRINT",EDGE,{"derivedFrom":sQuery(id+"F2.wireOp",EDGE,"E161.MirrorCS")}),1.0]])]});
            var Q5;
            Q5=makeQuery(id+"F2.imprint","IMPRINT",FACE,{"disambiguationData":[TD([[makeQuery(id+"F2.imprint","IMPRINT",EDGE,{"derivedFrom":sQuery(id+"F2.wireOp",EDGE,"E153.MirrorCS")}),1.0]])]});
            var Q6;
            Q6=makeQuery(id+"F2.imprint","IMPRINT",FACE,{"disambiguationData":[TD([[makeQuery(id+"F2.imprint","IMPRINT",EDGE,{"derivedFrom":sQuery(id+"F2.wireOp",EDGE,"E156.MirrorCS")}),1.0]])]});
            var Q7;
            Q7=makeQuery(id+"F2.imprint","IMPRINT",FACE,{"disambiguationData":[TD([[makeQuery(id+"F2.imprint","IMPRINT",EDGE,{"derivedFrom":sQuery(id+"F2.wireOp",EDGE,"E272")}),-1.0]])]});
            var Q8;
            Q8=makeQuery(id+"F2.imprint","IMPRINT",FACE,{"disambiguationData":[TD([[makeQuery(id+"F2.imprint","IMPRINT",EDGE,{"derivedFrom":sQuery(id+"F2.wireOp",EDGE,"E20.MirrorCS")}),-1.0]])]});
            var Q9;
            Q9=makeQuery(id+"F2.imprint","IMPRINT",FACE,{"disambiguationData":[TD([[makeQuery(id+"F2.imprint","IMPRINT",EDGE,{"derivedFrom":sQuery(id+"F2.wireOp",EDGE,"E22.MirrorCS")}),-1.0]])]});
            var Q10;
            Q10=makeQuery(id+"F2.imprint","IMPRINT",FACE,{"disambiguationData":[TD([[makeQuery(id+"F2.imprint","IMPRINT",EDGE,{"derivedFrom":sQuery(id+"F2.wireOp",EDGE,"E27.MirrorCS")}),-1.0]])]});
            var Q11;
            Q11=makeQuery(id+"F2.imprint","IMPRINT",FACE,{"disambiguationData":[TD([[makeQuery(id+"F2.imprint","IMPRINT",EDGE,{"derivedFrom":sQuery(id+"F2.wireOp",EDGE,"E21.MirrorCS")}),-1.0]])]});
            var Q12;
            {var subQ2=sQuery(id+"F2.wireOp",EDGE,"E28.MirrorCS");Q12=makeQuery(id+"F2.imprint","IMPRINT",FACE,{"disambiguationData":[TD([[makeQuery(id+"F2.imprint","IMPRINT",EDGE,{"derivedFrom":subQ2}),-1.0]])]});}
            var Q13;
            Q13=makeQuery(id+"F2.imprint","IMPRINT",FACE,{"disambiguationData":[TD([[makeQuery(id+"F2.imprint","IMPRINT",EDGE,{"derivedFrom":sQuery(id+"F2.wireOp",EDGE,"E82.MirrorCS")}),-1.0]])]});
            var Q14;
            Q14=makeQuery(id+"F2.imprint","IMPRINT",FACE,{"disambiguationData":[TD([[makeQuery(id+"F2.imprint","IMPRINT",EDGE,{"derivedFrom":sQuery(id+"F2.wireOp",EDGE,"E81.MirrorCS")}),-1.0]])]});
            var Q15;
            Q15=makeQuery(id+"F2.imprint","IMPRINT",FACE,{"disambiguationData":[TD([[makeQuery(id+"F2.imprint","IMPRINT",EDGE,{"derivedFrom":sQuery(id+"F2.wireOp",EDGE,"E85.MirrorCS")}),-1.0]])]});
            var Q16;
            Q16=makeQuery(id+"F2.imprint","IMPRINT",FACE,{"disambiguationData":[TD([[makeQuery(id+"F2.imprint","IMPRINT",EDGE,{"derivedFrom":sQuery(id+"F2.wireOp",EDGE,"E83.MirrorCS")}),1.0]])]});
            var Q17;
            Q17=makeQuery(id+"F2.imprint","IMPRINT",FACE,{"disambiguationData":[TD([[makeQuery(id+"F2.imprint","IMPRINT",EDGE,{"derivedFrom":sQuery(id+"F2.wireOp",EDGE,"E281.MirrorCS")}),-1.0]])]});
            var Q18;
            Q18=makeQuery(id+"F2.imprint","IMPRINT",FACE,{"disambiguationData":[TD([[makeQuery(id+"F2.imprint","IMPRINT",EDGE,{"derivedFrom":sQuery(id+"F2.wireOp",EDGE,"E165.MirrorCS")}),-1.0]])]});
            var Q19;
            Q19=makeQuery(id+"F2.imprint","IMPRINT",FACE,{"disambiguationData":[TD([[makeQuery(id+"F2.imprint","IMPRINT",EDGE,{"derivedFrom":sQuery(id+"F2.wireOp",EDGE,"E152.MirrorCS")}),-1.0]])]});
            extrude(context, id + "F3", {"entities" : qUnion([Q0, Q1, Q2, Q3, Q4, Q5, Q6, Q7, Q8, Q9, Q10, Q11, Q12, Q13, Q14, Q15, Q16, Q17, Q18, Q19]), "operationType" : NewBodyOperationType.ADD, "depth" : 6.35 * mm});
        }
    });
